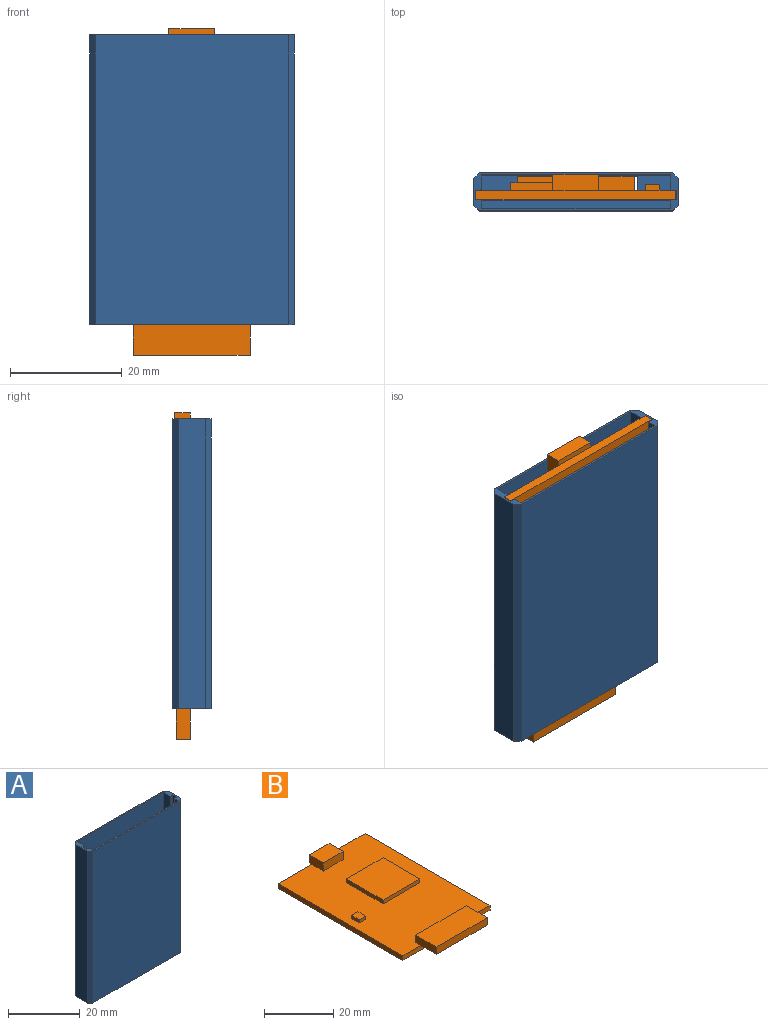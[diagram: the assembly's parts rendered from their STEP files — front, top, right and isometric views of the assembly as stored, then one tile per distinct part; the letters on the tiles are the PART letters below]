
ASSEMBLY  parts=2 mates=1
PART A: 30 faces, bbox 36.6x6.8x51.8 mm
  f0: plane 35.75x6.01mm, normal (0,0,1), area 139.6mm2, adj f1,f2,f3,f4,f12,f13,f14,f15
  f1: plane 51.4x1.7mm, normal (-1,0,0), area 87.4mm2, adj f0,f6,f20,f22
  f2: plane 51.4x33.75mm, normal (0,-1,0), area 1722.2mm2, adj f0,f6,f11,f16,f23
  f3: plane 51.4x33.75mm, normal (0,1,0), area 1734.8mm2, adj f0,f6,f18,f21
  f4: plane 51.4x1.7mm, normal (1,0,0), area 87.4mm2, adj f0,f6,f17,f19
  f5: plane 36.55x6.81mm, normal (0,0,-1), area 180.3mm2, adj f7,f8,f9,f10,f12,f13,f14,f15
  f6: plane 36.55x6.81mm, normal (0,0,1), area 40.6mm2, adj f1,f2,f3,f4,f7,f8,f9,f10
  f7: plane 51.8x4.81mm, normal (-1,0,0), area 249.2mm2, adj f5,f6,f26,f27
  f8: plane 51.8x34.55mm, normal (0,-1,0), area 1789.7mm2, adj f5,f6,f27,f29
  f9: plane 51.8x4.81mm, normal (1,0,0), area 249.2mm2, adj f5,f6,f28,f29
  f10: plane 51.8x34.55mm, normal (0,1,0), area 1777.1mm2, adj f5,f6,f11,f26,f28
  f11: cylinder r=2mm len=4mm, axis (0,1,0), area 5mm2, adj f2,f10
  f12: plane 21.5x0.4mm, normal (0,-1,0), area 8.6mm2, adj f0,f5,f13,f15
  f13: plane 3.1x0.4mm, normal (-1,0,0), area 1.2mm2, adj f0,f5,f12,f14
  f14: plane 21.5x0.4mm, normal (0,1,0), area 8.6mm2, adj f0,f5,f13,f15
  f15: plane 3.1x0.4mm, normal (1,0,0), area 1.2mm2, adj f0,f5,f12,f14
  f16: plane 51.4x2.47mm, normal (1,0,0), area 127mm2, adj f0,f2,f6,f24
  f17: plane 51.4x0.75mm, normal (0,-1,0), area 38.5mm2, adj f0,f4,f6,f24
  f18: plane 51.4x1.39mm, normal (1,0,0), area 71.4mm2, adj f0,f3,f6,f25
  f19: plane 51.4x0.8mm, normal (0,1,0), area 41.1mm2, adj f0,f4,f6,f25
  f20: plane 51.4x1mm, normal (0,1,0), area 51.4mm2, adj f0,f1,f6,f21
  f21: plane 51.4x1.59mm, normal (-1,0,0), area 81.7mm2, adj f0,f3,f6,f20
  f22: plane 51.4x1mm, normal (0,-1,0), area 51.4mm2, adj f0,f1,f6,f23
  f23: plane 51.4x2.72mm, normal (-1,0,0), area 139.8mm2, adj f0,f2,f6,f22
  f24: cylinder r=0.25mm len=51.4mm, axis (0,0,-1), area 20.2mm2, adj f0,f6,f16,f17
  f25: cylinder r=0.2mm len=51.4mm, axis (0,0,1), area 16.1mm2, adj f0,f6,f18,f19
  f26: plane 51.8x1mm, normal (-0.71,0.71,0), area 73.3mm2, adj f5,f6,f7,f10
  f27: plane 51.8x1mm, normal (-0.71,-0.71,0), area 73.3mm2, adj f5,f6,f7,f8
  f28: plane 51.8x1mm, normal (0.71,0.71,0), area 73.3mm2, adj f5,f6,f9,f10
  f29: plane 51.8x1mm, normal (0.71,-0.71,0), area 73.3mm2, adj f5,f6,f8,f9
PART B: 28 faces, bbox 35.6x58.3x4.5 mm
  f0: plane 51x35.6mm, normal (0,0,1), area 1498.7mm2, adj f1,f2,f3,f4,f7,f8,f9,f13
  f1: plane 51x1.68mm, normal (-1,0,0), area 85.7mm2, adj f0,f2,f4,f5
  f2: plane 35.6x1.68mm, normal (0,-1,0), area 59.8mm2, adj f0,f1,f3,f5,f6
  f3: plane 51x1.68mm, normal (1,0,0), area 85.7mm2, adj f0,f2,f4,f5
  f4: plane 35.6x1.68mm, normal (0,1,0), area 59.8mm2, adj f0,f1,f3,f5,f17
  f5: plane 51x35.6mm, normal (0,0,-1), area 1815.6mm2, adj f1,f2,f3,f4
  f6: plane 20.83x6.33mm, normal (0,0,-1), area 131.9mm2, adj f2,f7,f9,f10
  f7: plane 8.5x2.56mm, normal (1,0,0), area 21.8mm2, adj f0,f6,f8,f10,f11
  f8: plane 20.83x2.56mm, normal (0,1,0), area 53.3mm2, adj f0,f7,f9,f11
  f9: plane 8.5x2.56mm, normal (-1,0,0), area 21.8mm2, adj f0,f6,f8,f10,f11
  f10: plane 20.83x2.56mm, normal (0,-1,0), area 53.3mm2, adj f6,f7,f9,f11
  f11: plane 20.83x8.5mm, normal (0,0,1), area 177.1mm2, adj f7,f8,f9,f10
  f12: plane 8.1x2.84mm, normal (0,1,0), area 23mm2, adj f13,f15,f16,f17
  f13: plane 5.75x2.84mm, normal (-1,0,0), area 16.3mm2, adj f0,f12,f14,f16,f17
  f14: plane 8.1x2.84mm, normal (0,-1,0), area 23mm2, adj f0,f13,f15,f16
  f15: plane 5.75x2.84mm, normal (1,0,0), area 16.3mm2, adj f0,f12,f14,f16,f17
  f16: plane 8.1x5.75mm, normal (0,0,1), area 46.6mm2, adj f12,f13,f14,f15
  f17: plane 8.1x1mm, normal (0,0,-1), area 8.1mm2, adj f4,f12,f13,f15
  f18: plane 15x1.34mm, normal (0,1,0), area 20.1mm2, adj f0,f19,f21,f22
  f19: plane 15x1.34mm, normal (-1,0,0), area 20.1mm2, adj f0,f18,f20,f22
  f20: plane 15x1.34mm, normal (0,-1,0), area 20.1mm2, adj f0,f19,f21,f22
  f21: plane 15x1.34mm, normal (1,0,0), area 20.1mm2, adj f0,f18,f20,f22
  f22: plane 15x15mm, normal (0,0,1), area 225mm2, adj f18,f19,f20,f21
  f23: plane 2.55x1.1mm, normal (0,1,0), area 2.8mm2, adj f0,f24,f26,f27
  f24: plane 3.22x1.1mm, normal (-1,0,0), area 3.5mm2, adj f0,f23,f25,f27
  f25: plane 2.55x1.1mm, normal (0,-1,0), area 2.8mm2, adj f0,f24,f26,f27
  f26: plane 3.22x1.1mm, normal (1,0,0), area 3.5mm2, adj f0,f23,f25,f27
  f27: plane 3.22x2.55mm, normal (0,0,1), area 8.2mm2, adj f23,f24,f25,f26
PLACE A t=(-87.19,-176.21,-65.61)mm
PLACE B rot(axis=(0,0.71,0.71),180deg) t=(-51.19,-174.21,-64.71)mm
MATE pin_slot B.f3 <-> A.f4  axis (-1,0,0) through (-86.79,-173.37,-39.21)mm
